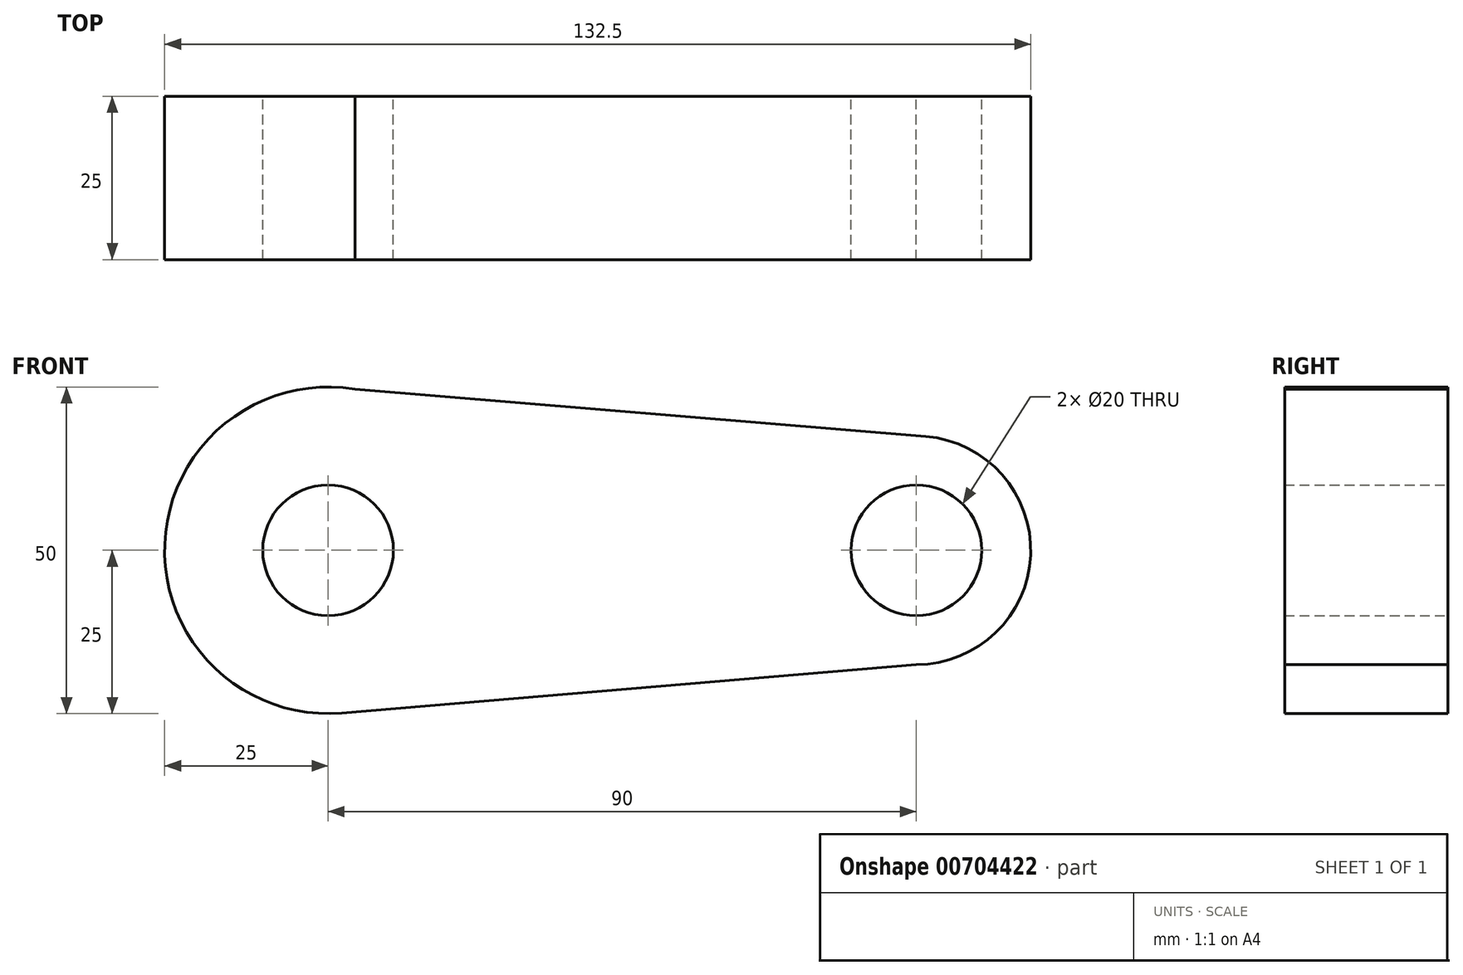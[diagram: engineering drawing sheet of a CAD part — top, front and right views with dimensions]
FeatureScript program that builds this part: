
annotation { "Feature Type Name" : "Feature", "Feature Type Description" : "" }
export const myFeature = defineFeature(function(context is Context, id is Id, definition is map)
    precondition{}
    {
        {
            var Q0;
            Q0=qCreatedBy(makeId("Front.planeOp"),FACE);
            var sketch = newSketch(context, id + "F0", { "sketchPlane" : qUnion([Q0])});
            skCircle(sketch, "E0", {"center": v(0, 0) * mm, "radius": 25 * mm});
            skCircle(sketch, "E1", {"center": v(90, 0) * mm, "radius": 17.5 * mm});
            skLineSegment(sketch, "E2", {"start": v(0, 0) * mm, "end": v(10, 0) * mm});
            skLineSegment(sketch, "E3", {"start": v(0, 25) * mm, "end": v(91.44, 17.44) * mm});
            skLineSegment(sketch, "E4", {"start": v(91.44, 17.44) * mm, "end": v(91.44, 17.44) * mm});
            skLineSegment(sketch, "E5", {"start": v(90, -17.5) * mm, "end": v(0, -25.09) * mm});
            skCircle(sketch, "E6", {"center": v(0, 0) * mm, "radius": 10 * mm});
            skCircle(sketch, "E7", {"center": v(90, 0) * mm, "radius": 10 * mm});
            skSolve(sketch);
        }
        {
            var Q0;
            Q0 = qSketchRegion(id + "F0", true);
            var Q1;
            {var subQ0=sQuery(id+"F0.wireOp",EDGE,"E5");var subQ1=sQuery(id+"F0.wireOp",EDGE,"E0");var subQ2=makeQuery(id+"F0.imprint","INTERSECT",VERTEX,{"derivedFrom":[subQ1,subQ0]});Q1=makeQuery(id+"F0.imprint","IMPRINT",FACE,{"disambiguationData":[TD([[makeQuery(id+"F0.imprint","IMPRINT",EDGE,{"disambiguationData":[TD([[subQ2,-1.0]])],"derivedFrom":subQ1}),-1.0]])]});}
            extrude(context, id + "F1", {"entities" : qUnion([Q0, Q1]), "depth" : 25 * mm, "offsetDistance" : 25 * mm});
        }
    });
